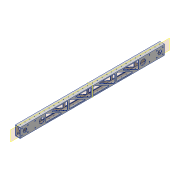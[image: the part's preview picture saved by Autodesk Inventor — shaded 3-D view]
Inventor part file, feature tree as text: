
AUTODESK INVENTOR PART (.ipt)
format: ipt  version: 2018 (Build 220112000, 112)  size: 371,712 bytes
history: native  units: in
note: dims shown in document units (in); Inventor stores cm internally (conversion verified against a paired STEP export)
features: sketch x8, extrude x6, hole x2, plane x2, mirror x2, shell x1, pattern_linear x1
ambient origin geometry x8: Origin, YZ Plane, XZ Plane, XY Plane, X Axis, Y Axis, Z Axis, Center Point
bodies: Solid1 (feature_tree)
feature tree (22):
  extrude  "Extrusion1"  Depth=2.0in
  shell  "Shell1"  Thickness=30.0in
  hole  "Hole1"  [1 undecoded]
  extrude  "Extrusion2"  Depth=1.0in
  extrude  "Extrusion4"  Depth=1.0in
  hole  "Hole5"  [1 undecoded]
  plane  "Work Plane1"
  mirror  "Mirror1"
  extrude  "Extrusion6"  Depth=1.0in
  extrude  "Extrusion7"  Depth=1.0in
  extrude  "Extrusion8"  Depth=4.925in
  pattern_linear  "Rectangular Pattern1"  Spacing1=0.375in  [1 undecoded]
  plane  "Work Plane2"
  mirror  "Mirror2"
  sketch  "Sketch1"  dims[d0=1.0in d1=2.0in d2=30.0in d3=0.0in]
  sketch  "Sketch2"  dims[d4=0.1in d5=0.5in]
  sketch  "Sketch6"  dims[d6=0.5in d7=14.5669in d9=1.0in d10=0.3937in d12=1.0in]
  sketch  "Sketch8"  dims[d14=0.1in d15=0.75in d16=0.375in d17=0.25in d18=0.5635in d19=2.0in d20=0.8108in d48=1.0in]
  sketch  "Sketch10"  dims[d49=1.0in d50=0.75in]
  sketch  "Sketch11"  dims[d51=1.0in d52=0.0in d57=1.0in]
  sketch  "Sketch12"  dims[d58=0.75in d59=1.0in]
  sketch  "Sketch13"  dims[d60=1.0in d61=0.0in d66=0.375in d67=0.375in d68=0.375in d69=0.375in d70=0.625in d72=1.25in d74=0.375in d75=1.5in d76=1.5in d77=0.375in d78=0.375in d79=0.375in d80=0.201in d81=0.75in d82=0.385in d83=0.25in d84=0.5635in d85=1.0in d86=0.8108in d87=1.0in d88=1.125in d89=1.125in d90=4.5in d91=4.5in d92=1.0in d93=1.0in d94=0.0in d100=1.0in d101=1.375in d102=1.0in d103=3.0in d104=0.5in d105=0.0in d106=0.25in d107=1.0in d108=1.375in d109=3.0in d110=1.3in d111=0.5in d112=0.0in d113=1.5748in d115=4.925in]
note: 3 required parameter values undecoded (feature->parameter linkage not recoverable at this tier; creation-order binding heuristic only, values carry confidence <= 0.55)
